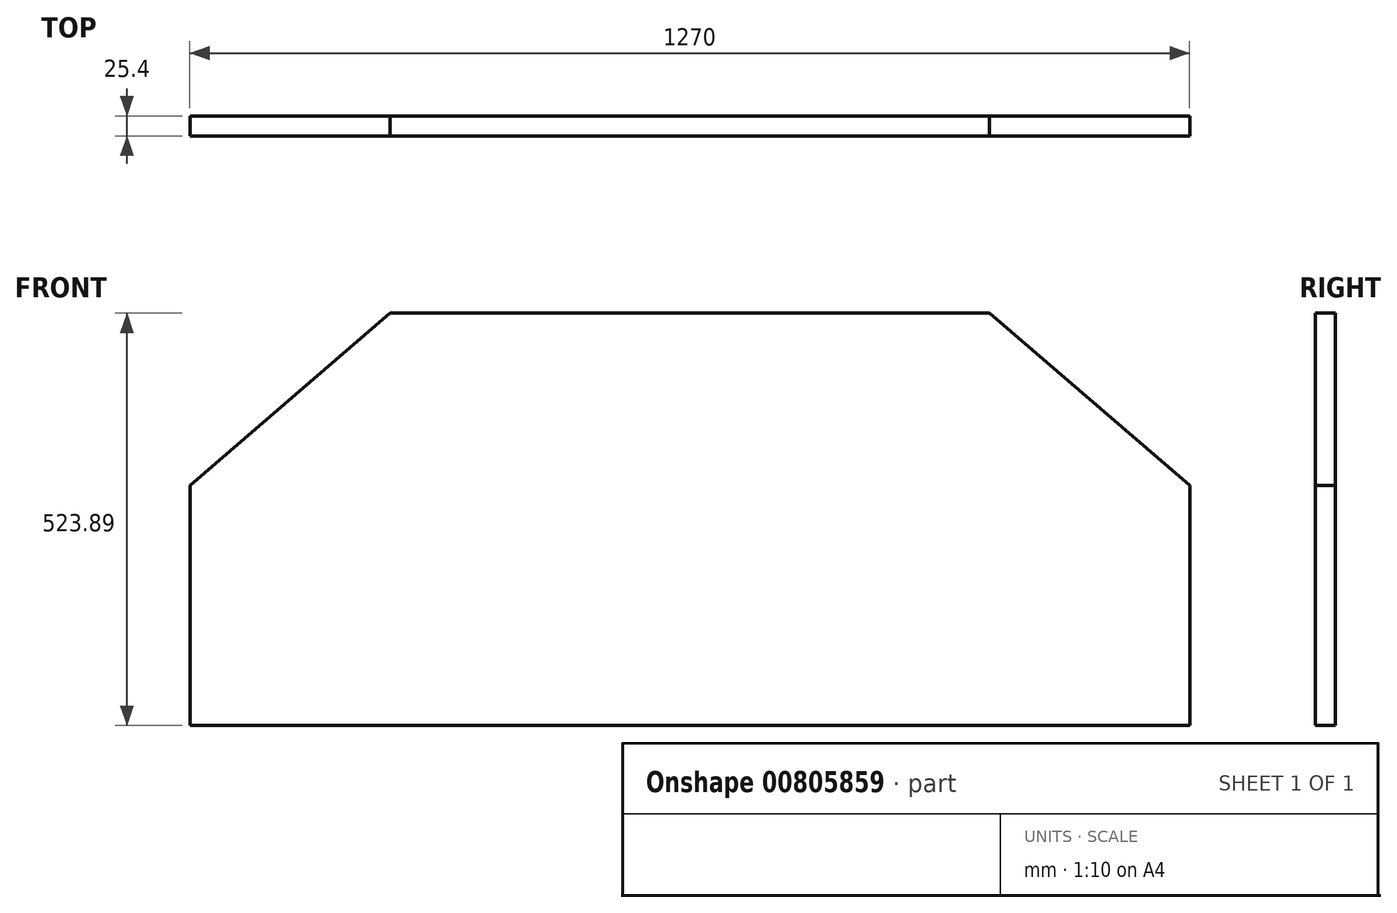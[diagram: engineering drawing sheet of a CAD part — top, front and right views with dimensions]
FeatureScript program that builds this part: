
annotation { "Feature Type Name" : "Feature", "Feature Type Description" : "" }
export const myFeature = defineFeature(function(context is Context, id is Id, definition is map)
    precondition{}
    {
        {
            var Q0;
            Q0=qCreatedBy(makeId("Front.planeOp"),FACE);
            var sketch = newSketch(context, id + "F0", { "sketchPlane" : qUnion([Q0])});
            skLineSegment(sketch, "E0", {"start": v(-601.59, 0) * mm, "end": v(668.41, 0) * mm});
            skLineSegment(sketch, "E1", {"start": v(-601.59, 0) * mm, "end": v(-601.59, 304.8) * mm});
            skLineSegment(sketch, "E2", {"start": v(668.41, 0) * mm, "end": v(668.41, 304.8) * mm});
            skLineSegment(sketch, "E3", {"start": v(-601.59, 304.8) * mm, "end": v(-347.08, 523.9) * mm});
            skLineSegment(sketch, "E4", {"start": v(-347.08, 523.9) * mm, "end": v(413.91, 523.9) * mm});
            skLineSegment(sketch, "E5", {"start": v(413.91, 523.9) * mm, "end": v(668.41, 304.8) * mm});
            skSolve(sketch);
        }
        {
            var Q0;
            Q0=makeQuery(id+"F0.imprint","IMPRINT",FACE,{"disambiguationData":[TD([[makeQuery(id+"F0.imprint","IMPRINT",EDGE,{"derivedFrom":sQuery(id+"F0.wireOp",EDGE,"E0")}),1.0]])]});
            var Q1;
            Q1=sQuery(id+"F0.wireOp",EDGE,"E4");
            var Q2;
            Q2=sQuery(id+"F0.wireOp",EDGE,"E0");
            extrude(context, id + "F1", {"entities" : qUnion([Q0]), "surfaceEntities" : qUnion([Q1, Q2]), "depth" : 25.4 * mm, "offsetDistance" : 25.4 * mm});
        }
    });
